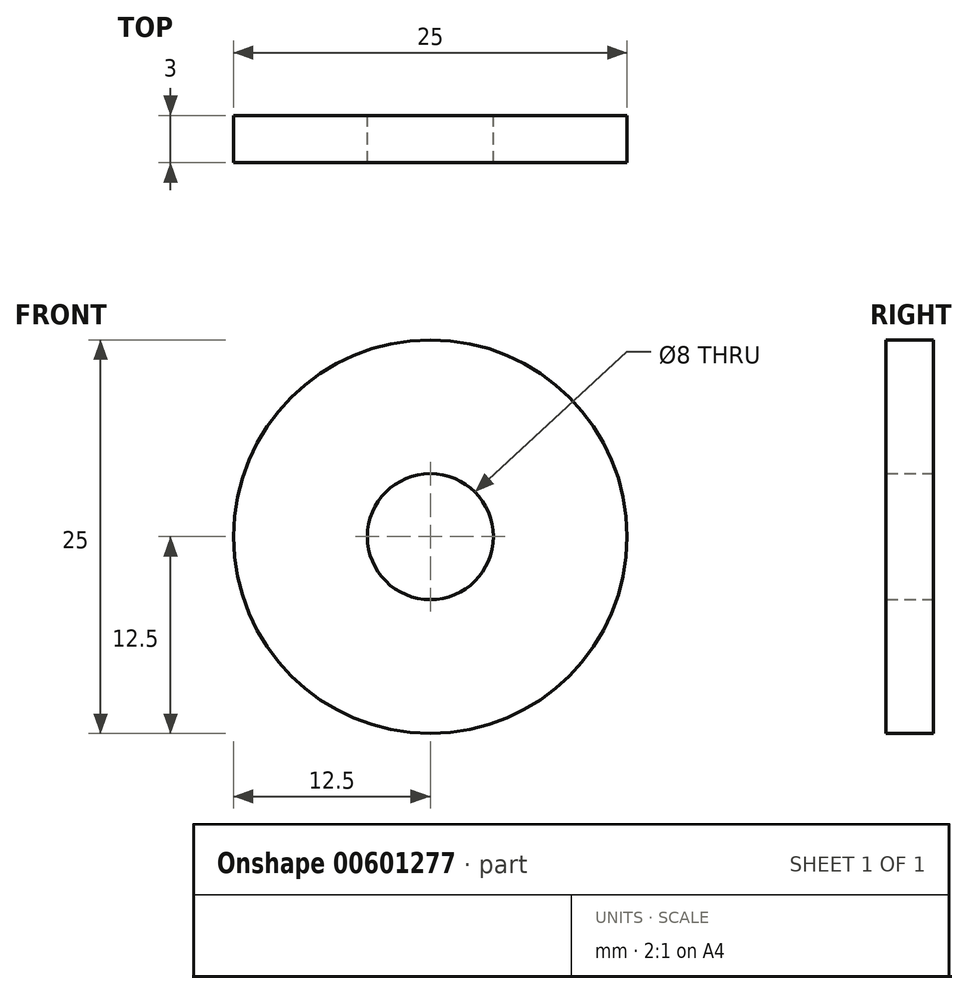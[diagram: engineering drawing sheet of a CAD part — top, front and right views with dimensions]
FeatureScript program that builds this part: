
annotation { "Feature Type Name" : "Feature", "Feature Type Description" : "" }
export const myFeature = defineFeature(function(context is Context, id is Id, definition is map)
    precondition{}
    {
        {
            var Q0;
            Q0=qCreatedBy(makeId("Front.planeOp"),FACE);
            var sketch = newSketch(context, id + "F0", { "sketchPlane" : qUnion([Q0])});
            skCircle(sketch, "E0", {"center": v(0, 0) * mm, "radius": 12.5 * mm});
            skCircle(sketch, "E1", {"center": v(0, 0) * mm, "radius": 4 * mm});
            skSolve(sketch);
        }
        {
            var Q0;
            Q0 = qSketchRegion(id + "F0", true);
            extrude(context, id + "F1", {"entities" : qUnion([Q0]), "endBound" : BoundingType.SYMMETRIC, "depth" : 3 * mm, "offsetDistance" : 25 * mm});
        }
    });
